# Revit family: PRD_FrankeWS_RcssdWshbsns_WashbasinUnit_ALIO320_ALIO325_ALIO330_ALIO335
name_source: partatom
category: Plumbing Fixtures
revit_build: Autodesk Revit 2018 (Build: 20190510_1515(x64)
units: mm (PartAtom-declared; Revit-internal decimal feet)

## family parameters
Cut with Voids When Loaded = Yes
Host = Face
OmniClass Number = 23.45.05.14.99
OmniClass Title = Other Sanitary Washing Plumbing Fixtures
Part Type = Normal
Room Calculation Point = No
Round Connector Dimension = Use Diameter
Shared = Yes

## types (4) — shared parameters
AssetType = Fixed
BowlFinish = Satin finish
BowlHeight = 40.00 mm
BowlPosition = Center
BowlShape = Rectangle
BowlWidth = 330.00 mm
Category = Pr_40_20_96_70, Recessed washbasins
Color = No colour
Default Elevation = 950 mm  [stored 3.1168 ft]
DiameterNominal = 40  [stored 0.131234 ft]
DrainSize = 40 mm  [stored 0.131234 ft]
DurationUnit = year
Features = vandal-resistant, complete unit with housing
Finish = Satin finished, brushed, welded
IfcExportAs = IfcSanitaryTerminalType
IfcExportType = WASHHANDBASIN
InletSize = DN 15
IntakeSize = 15  [stored 0.0492126 ft]
Manufacturer = KWC Group AG
ManufacturerName = KWC Group AG
ManufacturerURL = www.kwc.com
Material = Stainless steel
MaterialCode = 1.4301 Chrome Nickel steel V2A
Mounting = OTHER
NominalHeight = 530 mm  [stored 1.73885 ft]
NominalWidth = 475 mm  [stored 1.5584 ft]
NumberOfBowls = 1
NumberOfTapHoles = 0
Overflow = No
ProductInformation = https://pim.kwc.com
SiphonIncluded = No
TailorMade = No
TapLedge = No
TapMaterial = PRD_AR_StainlessSteel_SatinFinished
TypeOfMounting = Recessed mounting
TypeOfWasteKit = Welded perforated waste (non removable)
URL = www.kwc.com
Uniclass2015Code = Pr_40_20_96_70
Uniclass2015Title = Recessed washbasins
Uniclass2015Version = Products v1.17
Version = 1
WarrantyDurationUnit = year
WashHandBasinType = OTHER
WashbasinMaterial = PRD_AR_StainlessSteel_BrushedWelded
WasteKitIncluded = Yes
WasteSize = DN 40
zero-valued in all types: MountingOffset

## per-type parameters (varying)
| type | BIMObjectName | BackOffset | BowlDepth | Description | FrontOffset | GrossWeight | InletOffset | MaterialThickness | ModelNumber | Name | NetWeight | NominalDepth | Size | UpOffset | WasteHolePosition | WasteHoleProjection |
| ALIO320 | PRD_AR_RecessedWashbasins_WashbasinUnit_ALIO320 | 267 mm  [stored 0.875984 ft] | 370.00 mm | Washing unit for installation in the wall, vandal-resistant, particularly suitable for public toilet facilities in car parks and parking decks. Function components accessible via service room. Complete unit with housing, user area and bowl made of stainless steel, surface brushed, welded. For the delivery of water and soap with sequence control for hand dryer. | 100 mm  [stored 0.328084 ft] | 12.00 kg | 135 mm  [stored 0.442913 ft] | 1.20 mm | 2000101444 | ALL-IN-ONE Washbasin unit ALIO320 | 10.50 kg | 390 mm  [stored 1.27953 ft] | 475 x 530 x 390 mm (W x H x D) | 150 mm  [stored 0.492126 ft] | Center | 141.00 mm |
| ALIO330 | PRD_AR_RecessedWashbasins_WashbasinUnit_ALIO330 | 267 mm  [stored 0.875984 ft] | 370.00 mm | Washing unit for installation in the wall, vandal-resistant, particularly suitable for public toilet facilities in car parks and parking decks. Function components accessible via service room. Complete unit with housing, user area and bowl made of stainless steel, surface brushed, welded. Bowl projection 125 mm. For the delivery of water and soap. | 100 mm  [stored 0.328084 ft] | 23.00 kg | 135 mm  [stored 0.442913 ft] | 1.20 mm | 2000101445 | ALL-IN-ONE Washbasin unit ALIO330 | 21.85 kg | 390 mm  [stored 1.27953 ft] | 475 x 530 x 390 mm (W x H x D) | 150 mm  [stored 0.492126 ft] | Center |  |
| ALIO325 | PRD_AR_RecessedWashbasins_WashbasinUnit_ALIO325 | 170 mm  [stored 0.557743 ft] | 450.00 mm | Washing unit for installation in the wall, barrier-free version, vandal-resistant, particularly suitable for public toilet facilities in car parks and parking decks. Function components accessible via service room. Complete unit with housing, user area and bowl made of stainless steel, surface brushed, welded. Bowl projection 310 mm. For the delivery of water and soap with sequence control for hand dryer. | 285 mm  [stored 0.935039 ft] | 15.00 kg | 85 mm  [stored 0.278871 ft] |  | 2000101446 | ALL-IN-ONE Washbasin unit ALIO325 | 12.00 kg | 470 mm  [stored 1.54199 ft] | 475 x 530 x 470 mm (W x H x D) | 100 mm  [stored 0.328084 ft] | Center back |  |
| ALIO335 | PRD_AR_RecessedWashbasins_WashbasinUnit_ALIO335 | 170 mm  [stored 0.557743 ft] | 450.00 mm | Washing unit for installation in the wall, barrier-free version, vandal-resistant, particularly suitable for public toilet facilities in car parks and parking decks. Function components accessible via service room. Complete unit with housing, user area and bowl made of stainless steel, surface brushed, welded. Bowl projection 310 mm. For the delivery of water and soap. | 285 mm  [stored 0.935039 ft] | 20.00 kg | 85 mm  [stored 0.278871 ft] |  | 2000101447 | ALL-IN-ONE Washbasin unit ALIO335 | 18.00 kg | 470 mm  [stored 1.54199 ft] | 475 x 530 x 470 mm (W x H x D) | 100 mm  [stored 0.328084 ft] | Center back |  |

note: column(s) folded — value = type name in every type: Model, ModelReference

note: [stored X ft] marks values corroborated as IEEE doubles in the binary element streams (Revit-internal decimal feet)

## geometry (parser evidence)
native form markers: Sweep x11
no freeform markers — native parametric forms only
